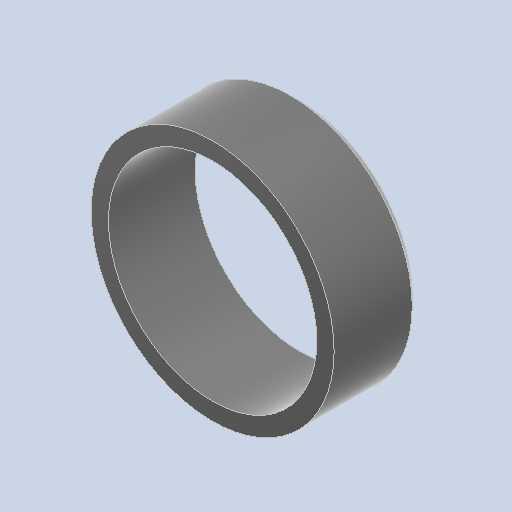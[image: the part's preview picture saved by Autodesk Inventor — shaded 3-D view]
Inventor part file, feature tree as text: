
AUTODESK INVENTOR PART (.ipt)
format: ipt  version: 2023 (Build 270158030, 158C)  size: 114,688 bytes
history: native  units: mm
features: extrude x1, chamfer x1, sketch x1
ambient origin geometry x8: Origin, YZ Plane, XZ Plane, XY Plane, X Axis, Y Axis, Z Axis, Center Point
bodies: Solid1 (feature_tree)
feature tree (3):
  extrude  "Extrusion1"  Depth=5.0mm
  chamfer  "Chamfer1"  Distance=5.0mm
  sketch  "Sketch1"  dims[d0=12.0mm d1=14.0mm d2=5.0mm d3=0.0mm d4=0.5mm d5=2.5mm d6=45.0deg]
